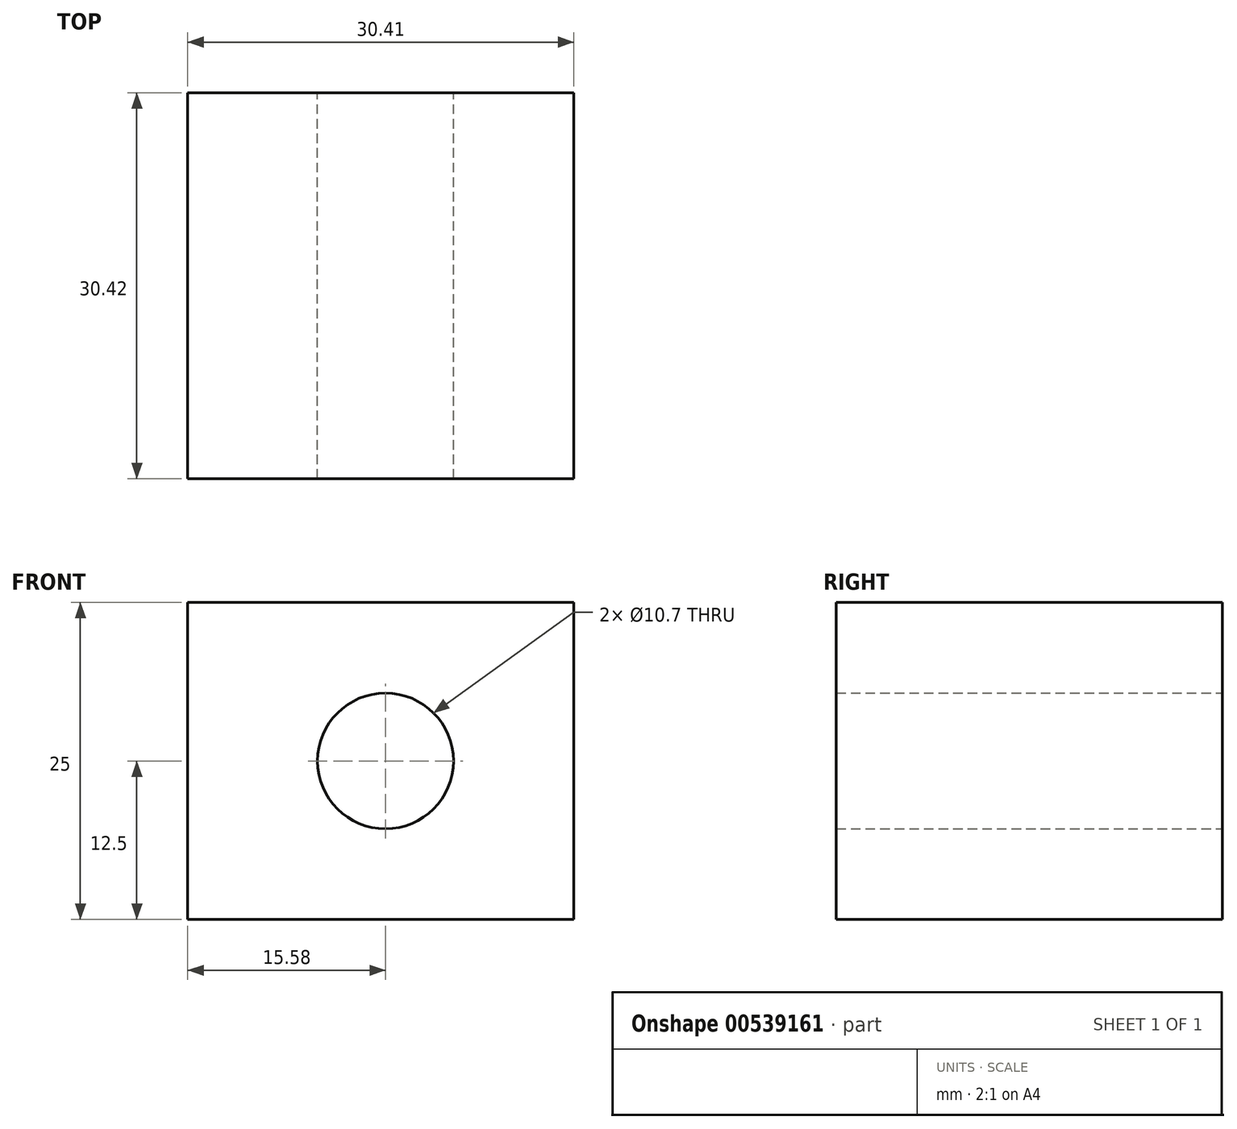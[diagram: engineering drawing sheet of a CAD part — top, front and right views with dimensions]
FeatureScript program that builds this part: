
annotation { "Feature Type Name" : "Feature", "Feature Type Description" : "" }
export const myFeature = defineFeature(function(context is Context, id is Id, definition is map)
    precondition{}
    {
        {
            var Q0;
            Q0=qCreatedBy(makeId("Top.planeOp"),FACE);
            var sketch = newSketch(context, id + "F0", { "sketchPlane" : qUnion([Q0])});
            skLineSegment(sketch, "E0.bottom", {"start": v(-15.58, 14.59) * mm, "end": v(14.83, 14.59) * mm});
            skLineSegment(sketch, "E0.top", {"start": v(-15.58, -15.83) * mm, "end": v(14.83, -15.83) * mm});
            skLineSegment(sketch, "E0.left", {"start": v(-15.58, 14.59) * mm, "end": v(-15.58, -15.83) * mm});
            skLineSegment(sketch, "E0.right", {"start": v(14.83, 14.59) * mm, "end": v(14.83, -15.83) * mm});
            skSolve(sketch);
        }
        {
            var Q0;
            Q0 = qSketchRegion(id + "F0", true);
            extrude(context, id + "F1", {"entities" : qUnion([Q0]), "endBound" : BoundingType.SYMMETRIC, "depth" : 25 * mm, "offsetDistance" : 25 * mm});
        }
        {
            var Q0;
            Q0=qCreatedBy(makeId("Front.planeOp"),FACE);
            var sketch = newSketch(context, id + "F2", { "sketchPlane" : qUnion([Q0])});
            skCircle(sketch, "E1", {"center": v(0, 0) * mm, "radius": 5.35 * mm});
            skSolve(sketch);
        }
        {
            var Q0;
            Q0 = qSketchRegion(id + "F2", true);
            extrude(context, id + "F3", {"entities" : qUnion([Q0]), "operationType" : NewBodyOperationType.REMOVE, "endBound" : BoundingType.SYMMETRIC, "depth" : 100 * mm, "offsetDistance" : 25 * mm});
        }
    });
